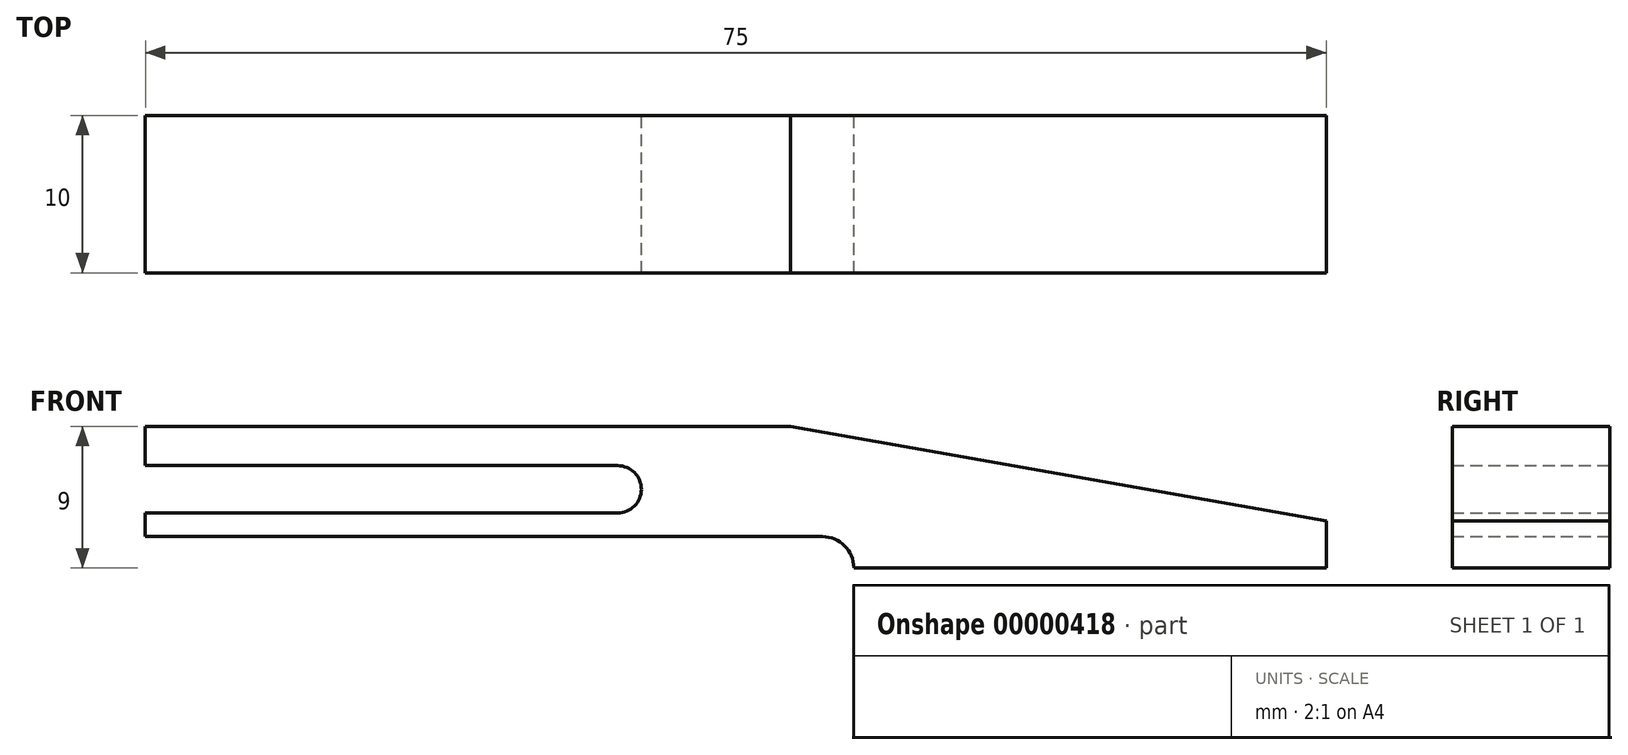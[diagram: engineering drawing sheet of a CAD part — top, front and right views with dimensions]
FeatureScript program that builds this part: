
annotation { "Feature Type Name" : "Feature", "Feature Type Description" : "" }
export const myFeature = defineFeature(function(context is Context, id is Id, definition is map)
    precondition{}
    {
        {
            var Q0;
            Q0=qCreatedBy(makeId("Front.planeOp"),FACE);
            var sketch = newSketch(context, id + "F0", { "sketchPlane" : qUnion([Q0])});
            skLineSegment(sketch, "E0", {"start": v(-54.38, 25.36) * mm, "end": v(18.13, -8.45) * mm, "construction": true});
            skLineSegment(sketch, "E1", {"start": v(0, 0) * mm, "end": v(24.81, 0) * mm, "construction": true});
            skLineSegment(sketch, "E2", {"start": v(-31.87, -8.45) * mm, "end": v(43.13, -8.45) * mm, "construction": true});
            skLineSegment(sketch, "E3.0.MirrorCS", {"start": v(-31.87, 8.45) * mm, "end": v(43.13, 8.45) * mm, "construction": true});
            skLineSegment(sketch, "E3.1.MirrorCS", {"start": v(-54.38, -25.36) * mm, "end": v(18.13, 8.45) * mm, "construction": true});
            skPoint(sketch, "E4", {"position": v(-18.13, 8.45) * mm});
            skSolve(sketch);
        }
        {
            var Q0;
            Q0=qCreatedBy(makeId("Front.planeOp"),FACE);
            var sketch = newSketch(context, id + "F1", { "sketchPlane" : qUnion([Q0])});
            skLineSegment(sketch, "E5", {"start": v(13.13, 3.45) * mm, "end": v(43.13, 3.45) * mm});
            skLineSegment(sketch, "E6", {"start": v(43.13, 3.45) * mm, "end": v(43.13, 6.45) * mm});
            skLineSegment(sketch, "E7", {"start": v(43.13, 6.45) * mm, "end": v(9.1, 12.45) * mm});
            skLineSegment(sketch, "E8", {"start": v(9.1, 12.45) * mm, "end": v(-31.87, 12.45) * mm});
            skLineSegment(sketch, "E9", {"start": v(-31.87, 12.45) * mm, "end": v(-31.87, 9.95) * mm});
            skLineSegment(sketch, "E10", {"start": v(-31.87, 9.95) * mm, "end": v(-1.87, 9.95) * mm});
            skLineSegment(sketch, "E11", {"start": v(-1.87, 9.95) * mm, "end": v(-1.87, 6.95) * mm, "construction": true});
            skLineSegment(sketch, "E12", {"start": v(-1.87, 6.95) * mm, "end": v(-31.87, 6.95) * mm});
            skLineSegment(sketch, "E13", {"start": v(-31.87, 6.95) * mm, "end": v(-31.87, 5.45) * mm});
            skLineSegment(sketch, "E14", {"start": v(-31.87, 5.45) * mm, "end": v(11.13, 5.45) * mm});
            skArc(sketch, "E15", {"start": v(13.13, 3.45) * mm, "mid": v(12.54, 4.87) * mm, "end": v(11.13, 5.45) * mm});
            skPoint(sketch, "E16", {"position": v(-1.87, 8.45) * mm});
            skArc(sketch, "E17", {"start": v(-1.87, 9.95) * mm, "mid": v(-0.37, 8.45) * mm, "end": v(-1.87, 6.95) * mm});
            skSolve(sketch);
        }
        {
            var Q0;
            Q0=makeQuery(id+"F1.imprint","IMPRINT",FACE,{"disambiguationData":[TD([[makeQuery(id+"F1.imprint","IMPRINT",EDGE,{"derivedFrom":sQuery(id+"F1.wireOp",EDGE,"E5")}),1.0]])]});
            extrude(context, id + "F2", {"entities" : qUnion([Q0]), "endBound" : BoundingType.SYMMETRIC, "depth" : 10 * mm});
        }
    });
